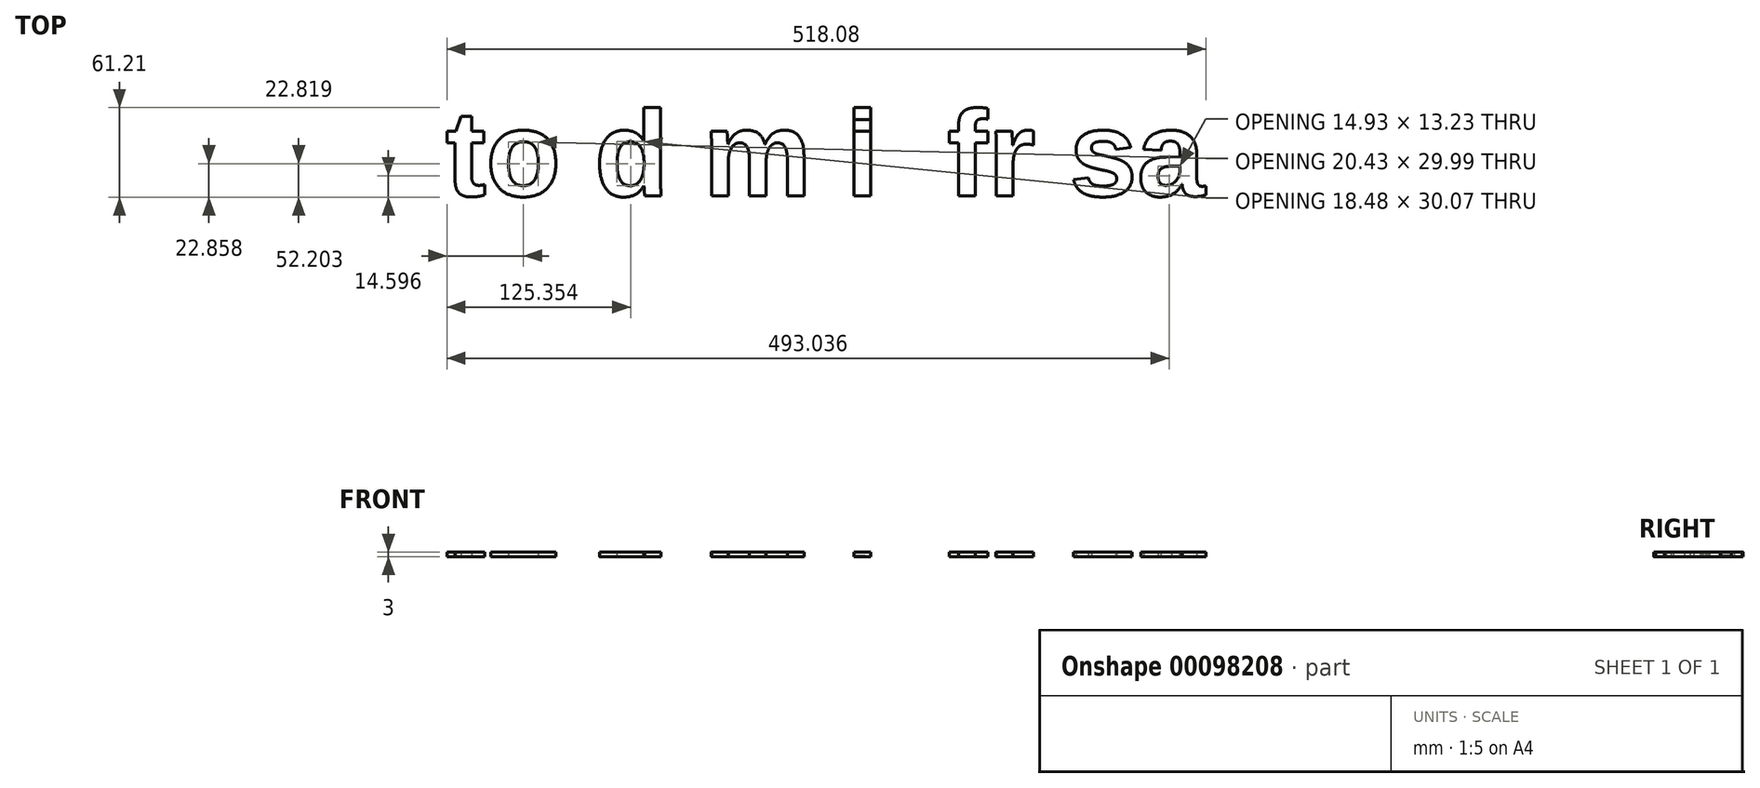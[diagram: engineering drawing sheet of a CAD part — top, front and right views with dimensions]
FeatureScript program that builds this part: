
annotation { "Feature Type Name" : "Feature", "Feature Type Description" : "" }
export const myFeature = defineFeature(function(context is Context, id is Id, definition is map)
    precondition{}
    {
        {
            var Q0;
            Q0=qCreatedBy(makeId("Top.planeOp"),FACE);
            var sketch = newSketch(context, id + "F0", { "sketchPlane" : qUnion([Q0])});
            skText(sketch, "E0", { "text": "to d m i  fr sa", "fontName": "Arimo-Bold.ttf"});
            skLineSegment(sketch, "E1", {"start": v(-125.64, 179.83) * mm, "end": v(393.46, 179.83) * mm, "construction": true});
            const initialGuessF0  = {"E0": [-0.12564, 0.15802, 1, 0, 0.06]};
            skSetInitialGuess(sketch, initialGuessF0);
            skSolve(sketch);
        }
        {
            var Q0;
            Q0 = qSketchRegion(id + "F0", true);
            extrude(context, id + "F1", {"entities" : qUnion([Q0]), "depth" : 3 * mm});
        }
        {
            var Q0;
            Q0=makeQuery(id+"F1.opExtrude","SWEPT_FACE",FACE,{"disambiguationData":[OSD([sQuery(id+"F0.wireOp",EDGE,"E0.sketch_text.stroke-90")])]});
            var sketch = newSketch(context, id + "F2", { "sketchPlane" : qUnion([Q0])});
            skLineSegment(sketch, "E2.bottom", {"start": v(-153.28, 0) * mm, "end": v(-164.71, 0) * mm});
            skLineSegment(sketch, "E2.top", {"start": v(-153.28, 1) * mm, "end": v(-164.71, 1) * mm});
            skLineSegment(sketch, "E2.left", {"start": v(-153.28, 0) * mm, "end": v(-153.28, 1) * mm});
            skLineSegment(sketch, "E2.right", {"start": v(-164.71, 0) * mm, "end": v(-164.71, 1) * mm});
            skSolve(sketch);
        }
        {
            var Q0;
            Q0=makeQuery(id+"F2.imprint","IMPRINT",FACE,{"disambiguationData":[TD([[makeQuery(id+"F2.imprint","IMPRINT",EDGE,{"derivedFrom":sQuery(id+"F2.wireOp",EDGE,"E2.bottom")}),-1.0]])]});
            extrude(context, id + "F3", {"entities" : qUnion([Q0]), "depth" : 8 * mm});
        }
    });
